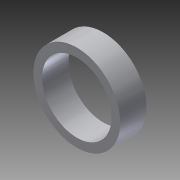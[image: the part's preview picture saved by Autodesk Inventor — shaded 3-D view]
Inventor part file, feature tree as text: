
AUTODESK INVENTOR PART (.ipt)
format: ipt  version: 2014 SP1 (Build 180222100, 222)  size: 84,480 bytes
history: native  units: in
note: dims shown in document units (in); Inventor stores cm internally (conversion verified against a paired STEP export)
features: extrude x1, sketch x1
ambient origin geometry x8: Origin, YZ Plane, XZ Plane, XY Plane, X Axis, Y Axis, Z Axis, Center Point
bodies: Solid1 (feature_tree)
feature tree (2):
  extrude  "Extrusion1"  Depth=0.19in
  sketch  "Sketch1"  dims[d0=0.5in d1=0.625in d2=0.19in d3=0.0in]
